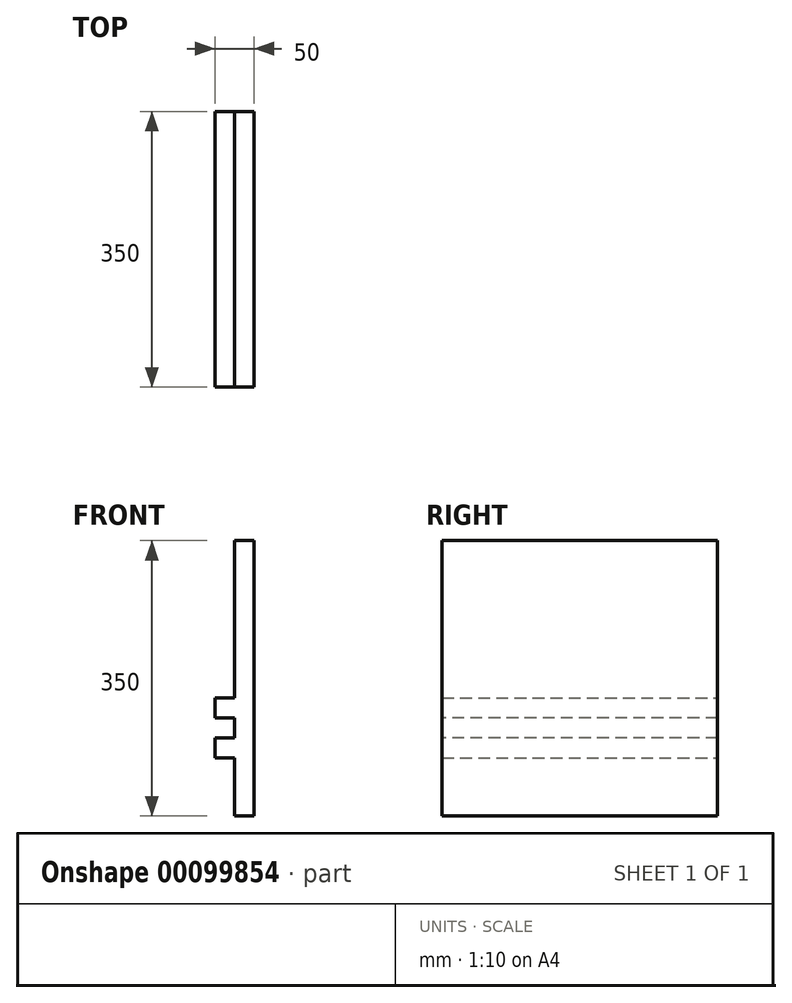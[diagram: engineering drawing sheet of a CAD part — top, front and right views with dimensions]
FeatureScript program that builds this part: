
annotation { "Feature Type Name" : "Feature", "Feature Type Description" : "" }
export const myFeature = defineFeature(function(context is Context, id is Id, definition is map)
    precondition{}
    {
        {
            var Q0;
            Q0=qCreatedBy(makeId("Right.planeOp"),FACE);
            var sketch = newSketch(context, id + "F0", { "sketchPlane" : qUnion([Q0])});
            skLineSegment(sketch, "E0.bottom", {"start": v(175, -175) * mm, "end": v(-175, -175) * mm});
            skLineSegment(sketch, "E0.top", {"start": v(175, 175) * mm, "end": v(-175, 175) * mm});
            skLineSegment(sketch, "E0.left", {"start": v(175, -175) * mm, "end": v(175, 175) * mm});
            skLineSegment(sketch, "E0.right", {"start": v(-175, -175) * mm, "end": v(-175, 175) * mm});
            skPoint(sketch, "E0.middle", {"position": v(0, 0) * mm});
            skSolve(sketch);
        }
        {
            var Q0;
            Q0=qSketchRegion(id+"F0",true);
            extrude(context, id + "F1", {"entities" : qUnion([Q0]), "depth" : 25 * mm});
        }
        {
            var Q0;
            Q0=makeQuery(id+"F1.opExtrude","CAP_FACE",FACE,{"disambiguationData":[OSD([sQuery(id+"F0.wireOp",EDGE,"E0.bottom"),sQuery(id+"F0.wireOp",EDGE,"E0.top"),sQuery(id+"F0.wireOp",EDGE,"E0.left"),sQuery(id+"F0.wireOp",EDGE,"E0.right")])],"isStart":true});
            var sketch = newSketch(context, id + "F2", { "sketchPlane" : qUnion([Q0])});
            skLineSegment(sketch, "E1.bottom", {"start": v(175, -25) * mm, "end": v(-175, -25) * mm});
            skLineSegment(sketch, "E1.top", {"start": v(-175, -50.4) * mm, "end": v(175, -50.4) * mm});
            skLineSegment(sketch, "E2", {"start": v(-175, -63.1) * mm, "end": v(175, -63.1) * mm, "construction": true});
            skPoint(sketch, "E1.left.end.orphan", {"position": v(175, -50.4) * mm});
            skPoint(sketch, "E3.orphan", {"position": v(175, -25) * mm});
            skLineSegment(sketch, "E4", {"start": v(-175, -25) * mm, "end": v(-175, -50.4) * mm});
            skLineSegment(sketch, "E5", {"start": v(175, -25) * mm, "end": v(175, -50.4) * mm});
            skPoint(sketch, "E6.MirrorP", {"position": v(175, -101.2) * mm});
            skPoint(sketch, "E7.MirrorP", {"position": v(175, -75.8) * mm});
            skLineSegment(sketch, "E8.MirrorCS", {"start": v(175, -101.2) * mm, "end": v(-175, -101.2) * mm});
            skLineSegment(sketch, "E9.MirrorCS", {"start": v(-175, -75.8) * mm, "end": v(175, -75.8) * mm});
            skLineSegment(sketch, "E10.MirrorCS", {"start": v(175, -101.2) * mm, "end": v(175, -75.8) * mm});
            skLineSegment(sketch, "E11.MirrorCS", {"start": v(-175, -101.2) * mm, "end": v(-175, -75.8) * mm});
            skSolve(sketch);
        }
        {
            var Q0;
            Q0=qSketchRegion(id+"F2",true);
            extrude(context, id + "F3", {"entities" : qUnion([Q0]), "operationType" : NewBodyOperationType.ADD, "depth" : 25 * mm});
        }
    });
